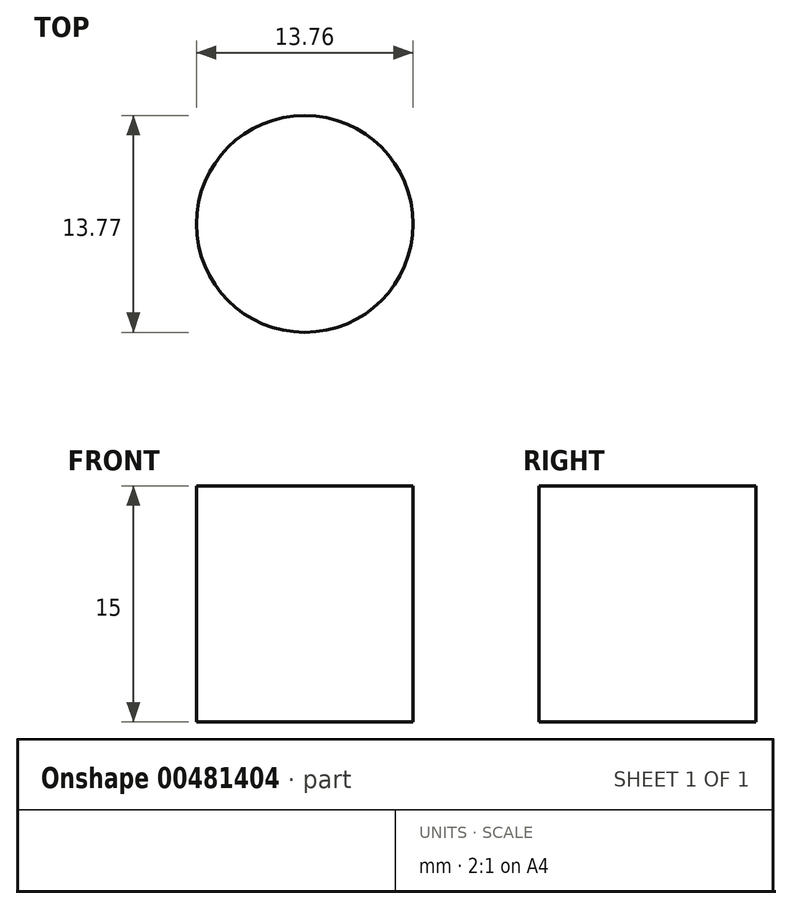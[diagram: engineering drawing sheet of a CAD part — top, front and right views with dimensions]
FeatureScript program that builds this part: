
annotation { "Feature Type Name" : "Feature", "Feature Type Description" : "" }
export const myFeature = defineFeature(function(context is Context, id is Id, definition is map)
    precondition{}
    {
        {
            var Q0;
            Q0=qCreatedBy(makeId("Top.planeOp"),FACE);
            var sketch = newSketch(context, id + "F0", { "sketchPlane" : qUnion([Q0])});
            skCircle(sketch, "E0", {"center": v(0, -8.24) * mm, "radius": 6.88 * mm});
            skSolve(sketch);
        }
        {
            var Q0;
            Q0 = qSketchRegion(id + "F0", true);
            extrude(context, id + "F1", {"entities" : qUnion([Q0]), "depth" : 15 * mm});
        }
    });
